# Revit family: IS_Mara_A9015_BIM_FR
name_source: partatom
category: Plumbing Fixtures
revit_build: Autodesk Revit 2017 (Build: 20160225_1515(x64)
units: mm (PartAtom-declared; Revit-internal decimal feet)

## family parameters
Always vertical = No
Cut with Voids When Loaded = No
OmniClass Number = 23.45.55.17
OmniClass Title = Mixing Faucets
Part Type = Normal
Room Calculation Point = No
Round Connector Dimension = Use Diameter
Shared = No
Work Plane-Based = No

## types (1)
- A9015 - Mitigeur douche mural
    Accessoires = www.idealstandard.be
    Assembly Code = C1030200
    Auteur = Ideal Standard
    BOSUseNativeGeometries = 1
    Caractéristiques = Mitigeur douche mural
    CodeBarre = 3800861012252
    ConseilsDInstallation = www.idealstandard.be
    Couleur = chromé
    CoûtDeRemplacement = 0
    DateDeCréation = 2018_08_15
    Description = Mitigeur douche mural
    Dimensions = 96 x 220 x 182
    DuréeDeGarantieDesPièces = 5
    DuréeGarantie = year
    DébitL/Mn = Litres
    DétailGarantie = Manufacturers Warranty
    Espace = Internal
    Finition = chromé
    Forme = Sculptured
    Hauteur = 96 mm
    IfcExportAs = IfcValveType
    IfcExportType = FAUCET
    InformationsProduit = www.idealstandard.be
    Largeur = 220 mm
    LienUtile = www.idealstandard.be
    Longueur = 182 mm
    Manufacturer = www.idealstandard.be
    Marque = Ideal Standard
    Matériel = Laiton
    Model = A9015
    Nom = Mitigeur douche mural
    PoidsBrut = 2.007
    PoidsNet = 1.876
    PressionDeFonctionnement = 0
    Révision = 1
    TechnologieDeLaRobinetterie = PILLAR
    TypeDeRobinetterie = MIXED
    URL = www.idealstandard.be
    UrlDuFabricant = www.idealstandard.be
    UsageDeLaRobinetterie = LEVERHANDLE

## geometry (parser evidence)
native form markers: Sweep x3
no freeform markers — native parametric forms only
